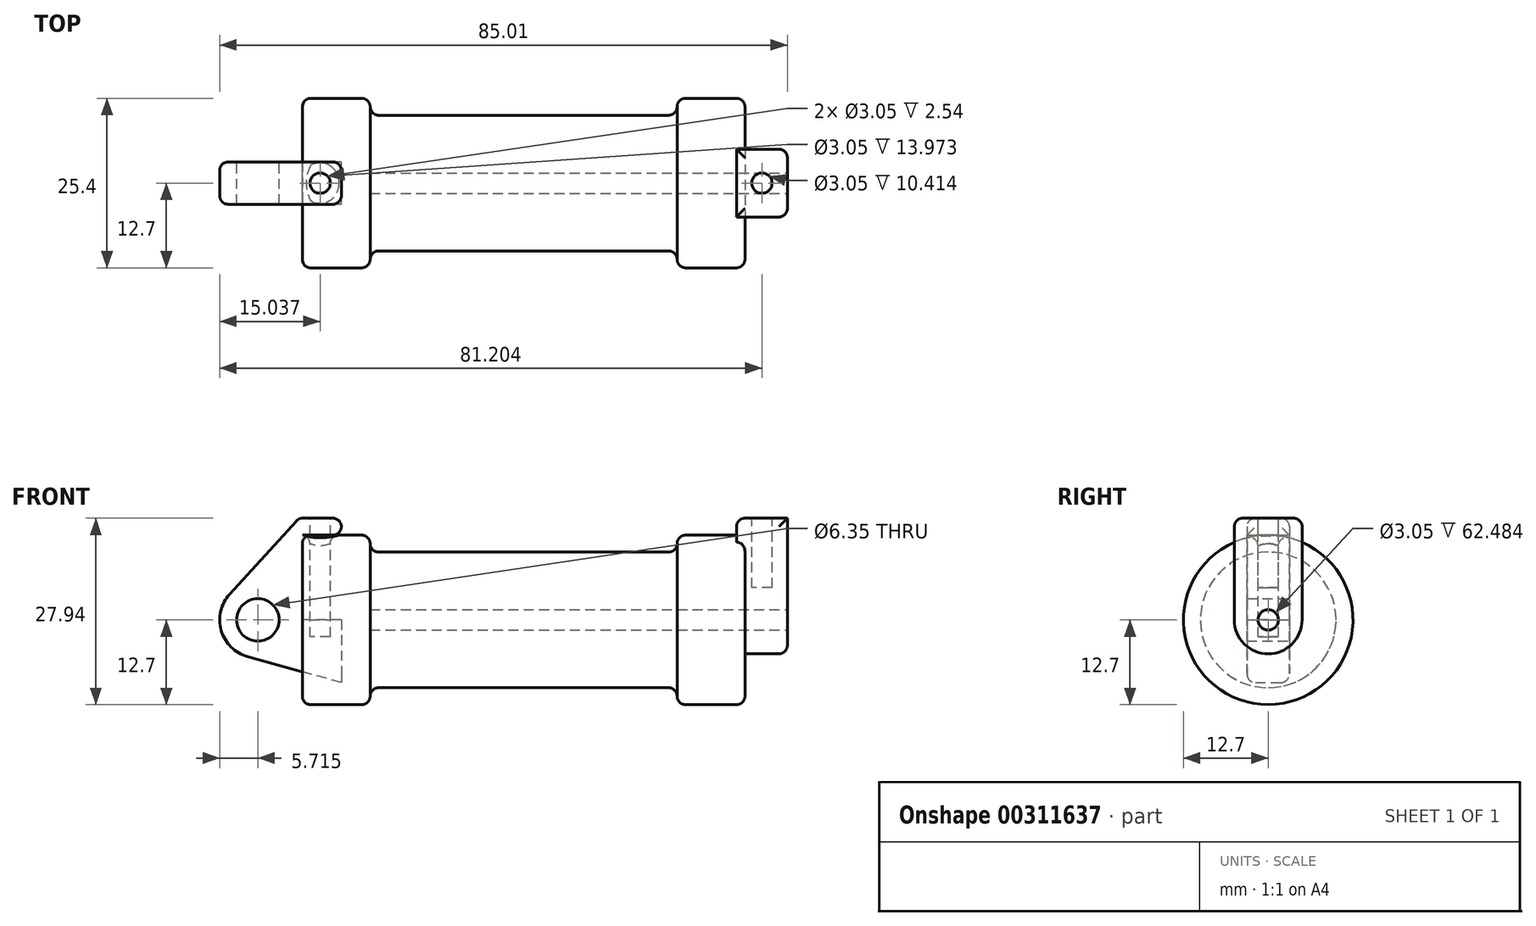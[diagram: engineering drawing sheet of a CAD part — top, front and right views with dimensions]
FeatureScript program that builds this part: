
annotation { "Feature Type Name" : "Feature", "Feature Type Description" : "" }
export const myFeature = defineFeature(function(context is Context, id is Id, definition is map)
    precondition{}
    {
        {
            var Q0;
            Q0=qCreatedBy(makeId("Front.planeOp"),FACE);
            var sketch = newSketch(context, id + "F0", { "sketchPlane" : qUnion([Q0])});
            skLineSegment(sketch, "E0", {"start": v(0, 0) * mm, "end": v(0, 12.7) * mm});
            skLineSegment(sketch, "E1", {"start": v(0, 12.7) * mm, "end": v(10.16, 12.7) * mm});
            skLineSegment(sketch, "E2", {"start": v(10.16, 12.7) * mm, "end": v(10.16, 10.16) * mm});
            skLineSegment(sketch, "E3", {"start": v(10.16, 10.16) * mm, "end": v(56.13, 10.16) * mm});
            skLineSegment(sketch, "E4", {"start": v(56.13, 10.16) * mm, "end": v(56.13, 12.7) * mm});
            skLineSegment(sketch, "E5", {"start": v(56.13, 12.7) * mm, "end": v(66.3, 12.7) * mm});
            skLineSegment(sketch, "E6", {"start": v(66.3, 12.7) * mm, "end": v(66.3, 0) * mm});
            skLineSegment(sketch, "E7", {"start": v(66.3, 0) * mm, "end": v(0, 0) * mm});
            skLineSegment(sketch, "E8", {"start": v(5.84, 15.24) * mm, "end": v(-0.5, 15.24) * mm});
            skLineSegment(sketch, "E9", {"start": v(-0.5, 15.24) * mm, "end": v(-10.88, 3.85) * mm});
            skLineSegment(sketch, "E10", {"start": v(0, 0) * mm, "end": v(-6.65, 0) * mm});
            skCircle(sketch, "E11", {"center": v(-6.65, 0) * mm, "radius": 5.72 * mm});
            skCircle(sketch, "E12", {"center": v(-6.65, 0) * mm, "radius": 3.18 * mm});
            skLineSegment(sketch, "E13", {"start": v(5.84, 15.24) * mm, "end": v(5.84, -9.4) * mm});
            skLineSegment(sketch, "E14", {"start": v(5.84, -9.4) * mm, "end": v(-8.18, -5.5) * mm});
            skSolve(sketch);
        }
        {
            var Q0;
            {var subQ0=sQuery(id+"F0.wireOp",EDGE,"E2");Q0=makeQuery(id+"F0.imprint","IMPRINT",FACE,{"disambiguationData":[TD([[makeQuery(id+"F0.imprint","IMPRINT",EDGE,{"derivedFrom":subQ0}),-1.0]])]});}
            var Q1;
            {var subQ0=sQuery(id+"F0.wireOp",EDGE,"E0");Q1=makeQuery(id+"F0.imprint","IMPRINT",FACE,{"disambiguationData":[TD([[makeQuery(id+"F0.imprint","IMPRINT",EDGE,{"derivedFrom":subQ0}),-1.0]])]});}
            var Q2;
            Q2=sQuery(id+"F0.wireOp",EDGE,"E7");
            revolve(context, id + "F1", {"entities" : qUnion([Q0, Q1]), "axis" : qUnion([Q2]), "revolveType" : RevolveType.FULL});
        }
        {
            var Q0;
            {var subQ1=sQuery(id+"F0.wireOp",EDGE,"E0");Q0=makeQuery(id+"F0.imprint","IMPRINT",FACE,{"disambiguationData":[TD([[makeQuery(id+"F0.imprint","IMPRINT",EDGE,{"derivedFrom":subQ1}),1.0]])]});}
            var Q1;
            {var subQ5=sQuery(id+"F0.wireOp",EDGE,"E12");Q1=makeQuery(id+"F0.imprint","IMPRINT",FACE,{"disambiguationData":[TD([[makeQuery(id+"F0.imprint","IMPRINT",EDGE,{"derivedFrom":subQ5}),-1.0]])]});}
            var Q2;
            {var subQ0=sQuery(id+"F0.wireOp",EDGE,"E14");Q2=makeQuery(id+"F0.imprint","IMPRINT",FACE,{"disambiguationData":[TD([[makeQuery(id+"F0.imprint","IMPRINT",EDGE,{"derivedFrom":subQ0}),-1.0]])]});}
            extrude(context, id + "F2", {"entities" : qUnion([Q0, Q1, Q2]), "endBound" : BoundingType.SYMMETRIC, "depth" : 6.35 * mm});
        }
        {
            var Q0;
            Q0=makeQuery(id+"F1.opRevolve","SWEPT_FACE",FACE,{"disambiguationData":[OSD([sQuery(id+"F0.wireOp",EDGE,"E6")])]});
            var sketch = newSketch(context, id + "F3", { "sketchPlane" : qUnion([Q0])});
            skCircle(sketch, "E15", {"center": v(0, 0) * mm, "radius": 1.52 * mm});
            skCircle(sketch, "E16", {"center": v(0, 0) * mm, "radius": 5.08 * mm});
            skLineSegment(sketch, "E17", {"start": v(5.08, 0) * mm, "end": v(5.08, 15.24) * mm});
            skLineSegment(sketch, "E18", {"start": v(-5.08, 0) * mm, "end": v(-5.08, 15.24) * mm});
            skLineSegment(sketch, "E19", {"start": v(-5.08, 15.24) * mm, "end": v(5.08, 15.24) * mm});
            skSolve(sketch);
        }
        {
            var Q0;
            Q0=makeQuery(id+"F3.imprint","IMPRINT",FACE,{"disambiguationData":[TD([[makeQuery(id+"F3.imprint","IMPRINT",EDGE,{"derivedFrom":sQuery(id+"F3.wireOp",EDGE,"E15")}),1.0]])]});
            var Q1;
            Q1=makeQuery(id+"F1.opRevolve","SWEPT_FACE",FACE,{"disambiguationData":[OSD([sQuery(id+"F0.wireOp",EDGE,"E2")])]});
            extrude(context, id + "F4", {"entities" : qUnion([Q0]), "operationType" : NewBodyOperationType.REMOVE, "endBound" : BoundingType.UP_TO_SURFACE, "oppositeDirection" : true, "endBoundEntityFace" : qUnion([Q1]), "depth" : 25.4 * mm});
        }
        {
            var Q0;
            {var subQ0=sQuery(id+"F3.wireOp",EDGE,"E19");Q0=makeQuery(id+"F3.imprint","IMPRINT",FACE,{"disambiguationData":[TD([[makeQuery(id+"F3.imprint","IMPRINT",EDGE,{"derivedFrom":subQ0}),-1.0]])]});}
            var Q1;
            {var subQ0=sQuery(id+"F3.wireOp",EDGE,"E17");var subQ1=sQuery(id+"F3.wireOp",EDGE,"E16");var subQ2=makeQuery(id+"F3.imprint","INTERSECT",VERTEX,{"derivedFrom":[subQ1,subQ0]});Q1=makeQuery(id+"F3.imprint","IMPRINT",FACE,{"disambiguationData":[TD([[makeQuery(id+"F3.imprint","IMPRINT",EDGE,{"disambiguationData":[TD([[subQ2,-1.0]])],"derivedFrom":subQ1}),-1.0]])]});}
            var Q2;
            Q2=makeQuery(id+"F3.imprint","IMPRINT",FACE,{"disambiguationData":[TD([[makeQuery(id+"F3.imprint","IMPRINT",EDGE,{"derivedFrom":sQuery(id+"F3.wireOp",EDGE,"E15")}),-1.0]])]});
            extrude(context, id + "F5", {"entities" : qUnion([Q0, Q1, Q2]), "operationType" : NewBodyOperationType.ADD, "depth" : 6.35 * mm});
        }
        {
            var Q0;
            {var subQ0=sQuery(id+"F3.wireOp",EDGE,"E19");Q0=makeQuery(id+"F3.imprint","IMPRINT",FACE,{"disambiguationData":[TD([[makeQuery(id+"F3.imprint","IMPRINT",EDGE,{"derivedFrom":subQ0}),-1.0]])]});}
            var Q1;
            {var subQ0=sQuery(id+"F3.wireOp",EDGE,"E17");var subQ1=sQuery(id+"F3.wireOp",EDGE,"E16");var subQ2=makeQuery(id+"F3.imprint","INTERSECT",VERTEX,{"derivedFrom":[subQ1,subQ0]});Q1=makeQuery(id+"F3.imprint","IMPRINT",FACE,{"disambiguationData":[TD([[makeQuery(id+"F3.imprint","IMPRINT",EDGE,{"disambiguationData":[TD([[subQ2,-1.0]])],"derivedFrom":subQ1}),-1.0]])]});}
            var Q2;
            Q2=makeQuery(id+"F3.imprint","IMPRINT",FACE,{"disambiguationData":[TD([[makeQuery(id+"F3.imprint","IMPRINT",EDGE,{"derivedFrom":sQuery(id+"F3.wireOp",EDGE,"E15")}),-1.0]])]});
            extrude(context, id + "F6", {"entities" : qUnion([Q0, Q1, Q2]), "operationType" : NewBodyOperationType.ADD, "oppositeDirection" : true, "depth" : 1.27 * mm});
        }
        {
            var Q0;
            {var subQ0=sQuery(id+"F3.wireOp",EDGE,"E19");Q0=makeQuery(id+"F6.boolean.opBoolean","MERGE",FACE,{"derivedFrom":[makeQuery(id+"F5.opExtrude","SWEPT_FACE",FACE,{"disambiguationData":[OSD([subQ0])]}),makeQuery(id+"F6.opExtrude","SWEPT_FACE",FACE,{"disambiguationData":[OSD([subQ0])]})]});}
            var sketch = newSketch(context, id + "F7", { "sketchPlane" : qUnion([Q0])});
            skCircle(sketch, "E20", {"center": v(2.67, 0) * mm, "radius": 1.52 * mm});
            skCircle(sketch, "E21", {"center": v(68.83, 0) * mm, "radius": 1.52 * mm});
            skPoint(sketch, "E21.centerSnap0", {"position": v(65.02, 0) * mm});
            skPoint(sketch, "E21.centerSnap1", {"position": v(68.83, 5.08) * mm});
            skSolve(sketch);
        }
        {
            var Q0;
            Q0=makeQuery(id+"F7.imprint","IMPRINT",FACE,{"disambiguationData":[TD([[makeQuery(id+"F7.imprint","IMPRINT",EDGE,{"derivedFrom":sQuery(id+"F7.wireOp",EDGE,"E20")}),1.0]])]});
            extrude(context, id + "F8", {"entities" : qUnion([Q0]), "operationType" : NewBodyOperationType.REMOVE, "oppositeDirection" : true, "depth" : 17.78 * mm});
        }
        {
            var Q0;
            Q0=makeQuery(id+"F7.imprint","IMPRINT",FACE,{"disambiguationData":[TD([[makeQuery(id+"F7.imprint","IMPRINT",EDGE,{"derivedFrom":sQuery(id+"F7.wireOp",EDGE,"E21")}),1.0]])]});
            extrude(context, id + "F9", {"entities" : qUnion([Q0]), "operationType" : NewBodyOperationType.REMOVE, "oppositeDirection" : true, "depth" : 10.4 * mm});
        }
        {
            var Q0;
            Q0=makeQuery(id+"F1.opRevolve","SWEPT_FACE",FACE,{"disambiguationData":[OSD([sQuery(id+"F0.wireOp",EDGE,"E3")])]});
            fillet(context, id + "F10", {"entities" : qUnion([Q0]), "radius" : 1.27 * mm, "tangentPropagation" : true, "allowEdgeOverflow" : false});
        }
        {
            var Q0;
            Q0=makeQuery(id+"F2.opExtrude","SWEPT_FACE",FACE,{"disambiguationData":[OSD([sQuery(id+"F0.wireOp",EDGE,"E9")])]});
            var Q1;
            {var subQ0=sQuery(id+"F0.wireOp",EDGE,"E13");Q1=makeQuery(id+"F2.opExtrude","SWEPT_FACE",FACE,{"disambiguationData":[OSD([subQ0]),TDD([makeQuery(id+"F0.imprint","IMPRINT",EDGE,{"disambiguationData":[TD([[makeQuery(id+"F0.imprint","INTERSECT",VERTEX,{"derivedFrom":[sQuery(id+"F0.wireOp",EDGE,"E8"),subQ0]}),-1.0]])],"derivedFrom":subQ0})])]});}
            var Q2;
            Q2=makeQuery(id+"F2.opExtrude","CAP_EDGE",EDGE,{"disambiguationData":[OSD([sQuery(id+"F0.wireOp",EDGE,"E8")])],"isStart":false});
            var Q3;
            Q3=makeQuery(id+"F2.opExtrude","CAP_EDGE",EDGE,{"disambiguationData":[OSD([sQuery(id+"F0.wireOp",EDGE,"E8")])],"isStart":true});
            var Q4;
            Q4=makeQuery(id+"F1.opRevolve","SWEPT_FACE",FACE,{"disambiguationData":[OSD([sQuery(id+"F0.wireOp",EDGE,"E1")])]});
            fillet(context, id + "F11", {"entities" : qUnion([Q0, Q1, Q2, Q3, Q4]), "radius" : 1.27 * mm, "tangentPropagation" : true, "allowEdgeOverflow" : false});
        }
        {
            var Q0;
            {var subQ0=sQuery(id+"F0.wireOp",EDGE,"E5");var subQ1=sQuery(id+"F0.wireOp",EDGE,"E6");Q0=makeQuery(id+"F5.boolean.opBoolean","SPLIT",EDGE,{"disambiguationData":[topologyDisambiguationEdgeConnected([makeQuery(id+"F1.opRevolve","SWEPT_FACE",FACE,{"disambiguationData":[OSD([subQ1])]})])],"derivedFrom":makeQuery(id+"F1.opRevolve","SWEPT_EDGE",EDGE,{"disambiguationData":[OSD([subQ0,subQ1])]})});}
            var Q1;
            Q1=makeQuery(id+"F1.opRevolve","SWEPT_EDGE",EDGE,{"disambiguationData":[OSD([sQuery(id+"F0.wireOp",EDGE,"E4"),sQuery(id+"F0.wireOp",EDGE,"E5")])]});
            var Q2;
            {var subQ0=sQuery(id+"F3.wireOp",EDGE,"E19");var subQ1=sQuery(id+"F3.wireOp",EDGE,"E18");Q2=makeQuery(id+"F6.boolean.opBoolean","MERGE",EDGE,{"derivedFrom":[makeQuery(id+"F5.opExtrude","SWEPT_EDGE",EDGE,{"disambiguationData":[OSD([subQ1,subQ0])]}),makeQuery(id+"F6.opExtrude","SWEPT_EDGE",EDGE,{"disambiguationData":[OSD([subQ1,subQ0])]})]});}
            var Q3;
            Q3=makeQuery(id+"F5.opExtrude","CAP_EDGE",EDGE,{"disambiguationData":[OSD([sQuery(id+"F3.wireOp",EDGE,"E18")])],"isStart":false});
            var Q4;
            Q4=makeQuery(id+"F6.opExtrude","CAP_EDGE",EDGE,{"disambiguationData":[OSD([sQuery(id+"F3.wireOp",EDGE,"E19")])],"isStart":false});
            var Q5;
            {var subQ0=sQuery(id+"F3.wireOp",EDGE,"E19");var subQ1=sQuery(id+"F3.wireOp",EDGE,"E17");Q5=makeQuery(id+"F6.boolean.opBoolean","MERGE",EDGE,{"derivedFrom":[makeQuery(id+"F5.opExtrude","SWEPT_EDGE",EDGE,{"disambiguationData":[OSD([subQ1,subQ0])]}),makeQuery(id+"F6.opExtrude","SWEPT_EDGE",EDGE,{"disambiguationData":[OSD([subQ1,subQ0])]})]});}
            fillet(context, id + "F12", {"entities" : qUnion([Q0, Q1, Q2, Q3, Q4, Q5]), "radius" : 1.27 * mm, "tangentPropagation" : true, "allowEdgeOverflow" : false});
        }
    });
